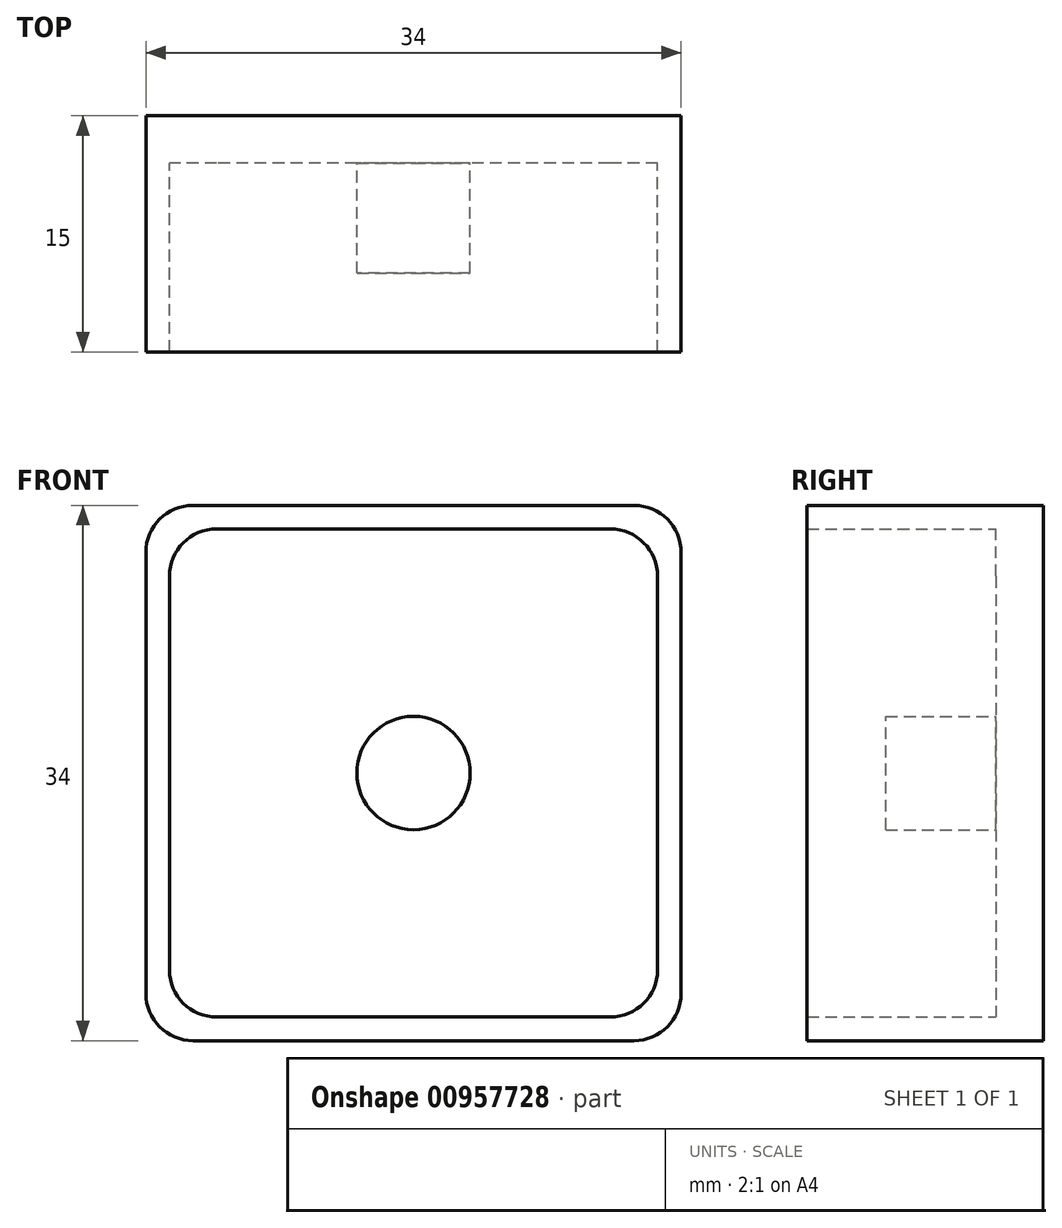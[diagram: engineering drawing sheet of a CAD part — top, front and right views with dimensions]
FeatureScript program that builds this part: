
annotation { "Feature Type Name" : "Feature", "Feature Type Description" : "" }
export const myFeature = defineFeature(function(context is Context, id is Id, definition is map)
    precondition{}
    {
        {
            var Q0;
            Q0=qCreatedBy(makeId("Front.planeOp"),FACE);
            var sketch = newSketch(context, id + "F0", { "sketchPlane" : qUnion([Q0])});
            skCircle(sketch, "E0", {"center": v(0, 0) * mm, "radius": 3.6 * mm});
            skLineSegment(sketch, "E1.bottom", {"start": v(12.5, 15.5) * mm, "end": v(-12.5, 15.5) * mm});
            skLineSegment(sketch, "E1.top", {"start": v(12.5, -15.5) * mm, "end": v(-12.5, -15.5) * mm});
            skLineSegment(sketch, "E1.left", {"start": v(15.5, 12.5) * mm, "end": v(15.5, -12.5) * mm});
            skLineSegment(sketch, "E1.right", {"start": v(-15.5, 12.5) * mm, "end": v(-15.5, -12.5) * mm});
            skPoint(sketch, "E2.visualSharp", {"position": v(-15.5, 15.5) * mm});
            skArc(sketch, "E2.filletArc", {"start": v(-12.5, 15.5) * mm, "mid": v(-14.62, 14.62) * mm, "end": v(-15.5, 12.5) * mm});
            skPoint(sketch, "E3.visualSharp", {"position": v(15.5, 15.5) * mm});
            skArc(sketch, "E3.filletArc", {"start": v(15.5, 12.5) * mm, "mid": v(14.62, 14.62) * mm, "end": v(12.5, 15.5) * mm});
            skPoint(sketch, "E4.visualSharp", {"position": v(15.5, -15.5) * mm});
            skArc(sketch, "E4.filletArc", {"start": v(12.5, -15.5) * mm, "mid": v(14.62, -14.62) * mm, "end": v(15.5, -12.5) * mm});
            skPoint(sketch, "E5.visualSharp", {"position": v(-15.5, -15.5) * mm});
            skArc(sketch, "E5.filletArc", {"start": v(-15.5, -12.5) * mm, "mid": v(-14.62, -14.62) * mm, "end": v(-12.5, -15.5) * mm});
            skLineSegment(sketch, "E6.bottom", {"start": v(-14, 17) * mm, "end": v(14, 17) * mm});
            skLineSegment(sketch, "E6.top", {"start": v(-14, -17) * mm, "end": v(14, -17) * mm});
            skLineSegment(sketch, "E6.left", {"start": v(-17, 14) * mm, "end": v(-17, -14) * mm});
            skLineSegment(sketch, "E6.right", {"start": v(17, 14) * mm, "end": v(17, -14) * mm});
            skPoint(sketch, "E7.visualSharp", {"position": v(-17, 17) * mm});
            skArc(sketch, "E7.filletArc", {"start": v(-14, 17) * mm, "mid": v(-16.12, 16.12) * mm, "end": v(-17, 14) * mm});
            skPoint(sketch, "E8.visualSharp", {"position": v(17, 17) * mm});
            skArc(sketch, "E8.filletArc", {"start": v(17, 14) * mm, "mid": v(16.12, 16.12) * mm, "end": v(14, 17) * mm});
            skPoint(sketch, "E9.visualSharp", {"position": v(17, -17) * mm});
            skArc(sketch, "E9.filletArc", {"start": v(14, -17) * mm, "mid": v(16.12, -16.12) * mm, "end": v(17, -14) * mm});
            skPoint(sketch, "E10.visualSharp", {"position": v(-17, -17) * mm});
            skArc(sketch, "E10.filletArc", {"start": v(-17, -14) * mm, "mid": v(-16.12, -16.12) * mm, "end": v(-14, -17) * mm});
            skSolve(sketch);
        }
        {
            var Q0;
            Q0=makeQuery(id+"F0.imprint","IMPRINT",FACE,{"disambiguationData":[TD([[makeQuery(id+"F0.imprint","IMPRINT",EDGE,{"derivedFrom":sQuery(id+"F0.wireOp",EDGE,"E0")}),-1.0]])]});
            extrude(context, id + "F1", {"entities" : qUnion([Q0]), "depth" : 3 * mm, "offsetDistance" : 25 * mm});
        }
        {
            var Q0;
            Q0=makeQuery(id+"F0.imprint","IMPRINT",FACE,{"disambiguationData":[TD([[makeQuery(id+"F0.imprint","IMPRINT",EDGE,{"derivedFrom":sQuery(id+"F0.wireOp",EDGE,"E0")}),1.0]])]});
            extrude(context, id + "F2", {"entities" : qUnion([Q0]), "operationType" : NewBodyOperationType.ADD, "depth" : 10 * mm, "offsetDistance" : 25 * mm});
        }
        {
            var Q0;
            Q0=makeQuery(id+"F0.imprint","IMPRINT",FACE,{"disambiguationData":[TD([[makeQuery(id+"F0.imprint","IMPRINT",EDGE,{"derivedFrom":sQuery(id+"F0.wireOp",EDGE,"E1.bottom")}),-1.0]])]});
            extrude(context, id + "F3", {"entities" : qUnion([Q0]), "operationType" : NewBodyOperationType.ADD, "depth" : 15 * mm, "offsetDistance" : 25 * mm});
        }
    });
